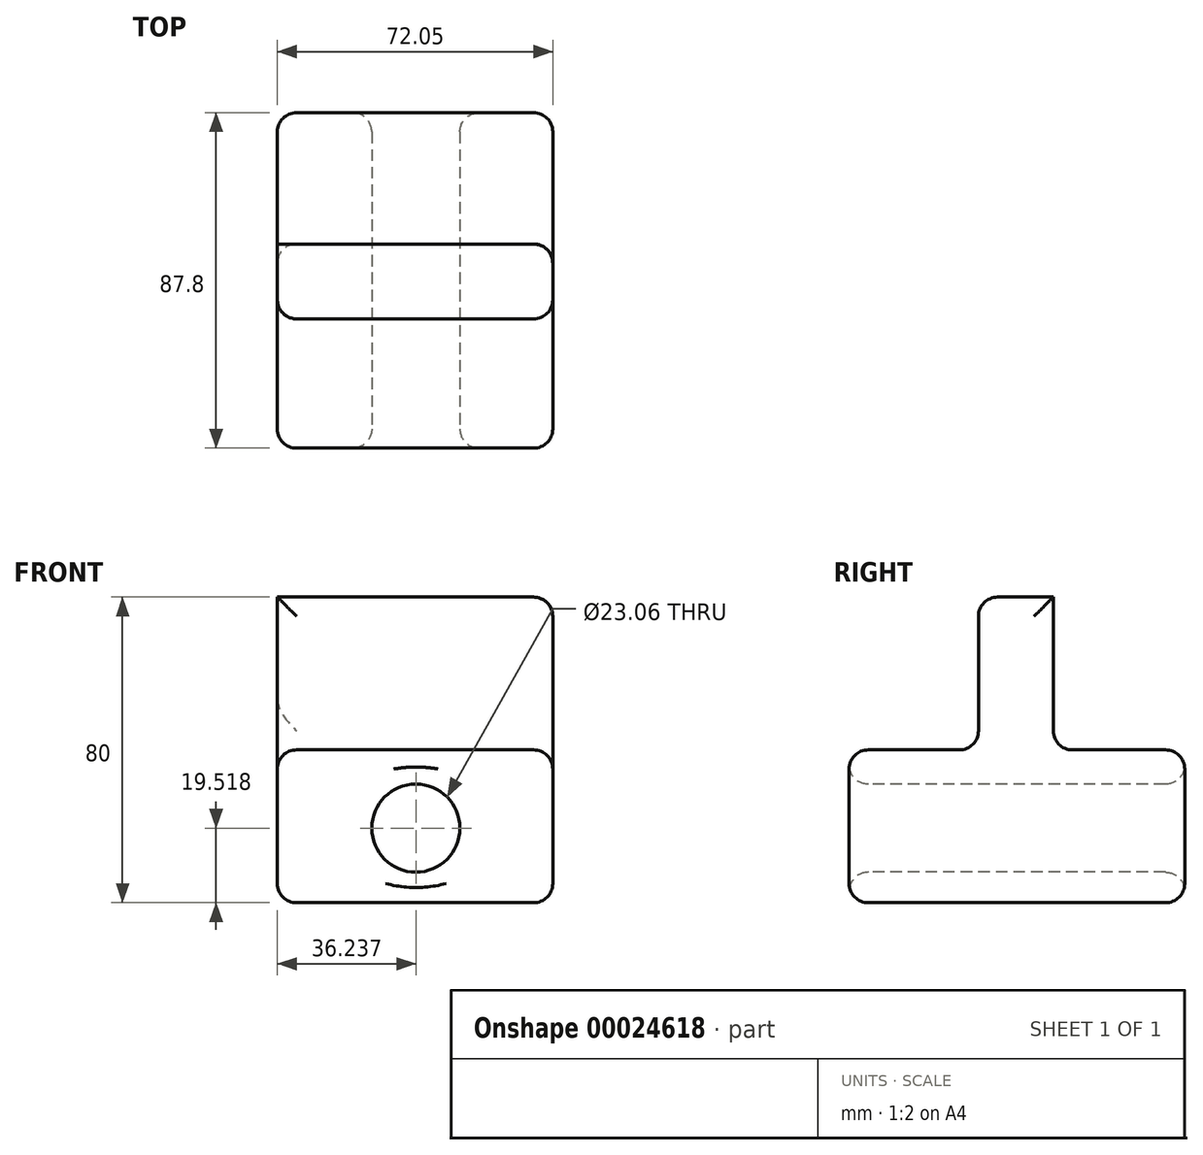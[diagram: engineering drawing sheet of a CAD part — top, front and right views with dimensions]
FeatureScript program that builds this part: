
annotation { "Feature Type Name" : "Feature", "Feature Type Description" : "" }
export const myFeature = defineFeature(function(context is Context, id is Id, definition is map)
    precondition{}
    {
        {
            var Q0;
            Q0=qCreatedBy(makeId("Top.planeOp"),FACE);
            var sketch = newSketch(context, id + "F0", { "sketchPlane" : qUnion([Q0])});
            skLineSegment(sketch, "E0.bottom", {"start": v(-59.89, -44.54) * mm, "end": v(12.16, -44.54) * mm});
            skLineSegment(sketch, "E0.top", {"start": v(-59.89, 43.26) * mm, "end": v(12.16, 43.26) * mm});
            skLineSegment(sketch, "E0.left", {"start": v(-59.89, -44.54) * mm, "end": v(-59.89, 43.26) * mm});
            skLineSegment(sketch, "E0.right", {"start": v(12.16, -44.54) * mm, "end": v(12.16, 43.26) * mm});
            skSolve(sketch);
        }
        {
            var Q0;
            Q0=makeQuery(id+"F0.imprint","IMPRINT",FACE,{"disambiguationData":[TD([[makeQuery(id+"F0.imprint","IMPRINT",EDGE,{"derivedFrom":sQuery(id+"F0.wireOp",EDGE,"E0.bottom")}),1.0]])]});
            extrude(context, id + "F1", {"entities" : qUnion([Q0]), "depth" : 40 * mm});
        }
        {
            var Q0;
            Q0=makeQuery(id+"F1.opExtrude","SWEPT_FACE",FACE,{"disambiguationData":[OSD([sQuery(id+"F0.wireOp",EDGE,"E0.bottom")])]});
            var sketch = newSketch(context, id + "F2", { "sketchPlane" : qUnion([Q0])});
            skCircle(sketch, "E1", {"center": v(-23.65, 19.52) * mm, "radius": 11.53 * mm});
            skSolve(sketch);
        }
        {
            var Q0;
            Q0=makeQuery(id+"F2.imprint","IMPRINT",FACE,{"disambiguationData":[TD([[makeQuery(id+"F2.imprint","IMPRINT",EDGE,{"derivedFrom":sQuery(id+"F2.wireOp",EDGE,"E1")}),1.0]])]});
            extrude(context, id + "F3", {"entities" : qUnion([Q0]), "operationType" : NewBodyOperationType.REMOVE, "endBound" : BoundingType.THROUGH_ALL, "oppositeDirection" : true, "depth" : 25 * mm});
        }
        {
            var Q0;
            Q0=makeQuery(id+"F1.opExtrude","CAP_FACE",FACE,{"disambiguationData":[OSD([sQuery(id+"F0.wireOp",EDGE,"E0.bottom"),sQuery(id+"F0.wireOp",EDGE,"E0.top"),sQuery(id+"F0.wireOp",EDGE,"E0.left"),sQuery(id+"F0.wireOp",EDGE,"E0.right")])],"isStart":false});
            var sketch = newSketch(context, id + "F4", { "sketchPlane" : qUnion([Q0])});
            skLineSegment(sketch, "E2.bottom", {"start": v(-59.89, -10.7) * mm, "end": v(12.16, -10.7) * mm});
            skLineSegment(sketch, "E2.top", {"start": v(-59.89, 8.88) * mm, "end": v(12.16, 8.88) * mm});
            skLineSegment(sketch, "E2.left", {"start": v(-59.89, -10.7) * mm, "end": v(-59.89, 8.88) * mm});
            skLineSegment(sketch, "E2.right", {"start": v(12.16, -10.7) * mm, "end": v(12.16, 8.88) * mm});
            skSolve(sketch);
        }
        {
            var Q0;
            Q0=makeQuery(id+"F4.imprint","IMPRINT",FACE,{"disambiguationData":[TD([[makeQuery(id+"F4.imprint","IMPRINT",EDGE,{"derivedFrom":sQuery(id+"F4.wireOp",EDGE,"E2.bottom")}),1.0]])]});
            extrude(context, id + "F5", {"entities" : qUnion([Q0]), "operationType" : NewBodyOperationType.ADD, "depth" : 40 * mm});
        }
        {
            var Q0;
            Q0=makeQuery(id+"F5.opExtrude","SWEPT_FACE",FACE,{"disambiguationData":[OSD([sQuery(id+"F4.wireOp",EDGE,"E2.bottom")])]});
            var Q1;
            {var subQ0=sQuery(id+"F0.wireOp",EDGE,"E0.bottom");var subQ1=sQuery(id+"F0.wireOp",EDGE,"E0.left");var subQ2=sQuery(id+"F0.wireOp",EDGE,"E0.right");Q1=makeQuery(id+"F5.boolean.opBoolean","SPLIT",FACE,{"disambiguationData":[TD([makeQuery(id+"F1.opExtrude","SWEPT_FACE",FACE,{"disambiguationData":[OSD([subQ0])]})])],"derivedFrom":makeQuery(id+"F1.opExtrude","CAP_FACE",FACE,{"disambiguationData":[OSD([subQ0,sQuery(id+"F0.wireOp",EDGE,"E0.top"),subQ1,subQ2])],"isStart":false})});}
            var Q2;
            Q2=makeQuery(id+"F1.opExtrude","SWEPT_FACE",FACE,{"disambiguationData":[OSD([sQuery(id+"F0.wireOp",EDGE,"E0.bottom")])]});
            var Q3;
            Q3=makeQuery(id+"F3.boolean.opBoolean","COPY",FACE,{"derivedFrom":makeQuery(id+"F3.opExtrude","SWEPT_FACE",FACE,{"disambiguationData":[OSD([sQuery(id+"F2.wireOp",EDGE,"E1")])]})});
            var Q4;
            Q4=makeQuery(id+"F5.boolean.opBoolean","MERGE",FACE,{"derivedFrom":[makeQuery(id+"F1.opExtrude","SWEPT_FACE",FACE,{"disambiguationData":[OSD([sQuery(id+"F0.wireOp",EDGE,"E0.right")])]}),makeQuery(id+"F5.opExtrude","SWEPT_FACE",FACE,{"disambiguationData":[OSD([sQuery(id+"F4.wireOp",EDGE,"E2.right")])]})]});
            var Q5;
            {var subQ0=sQuery(id+"F0.wireOp",EDGE,"E0.top");var subQ1=sQuery(id+"F0.wireOp",EDGE,"E0.left");var subQ2=sQuery(id+"F0.wireOp",EDGE,"E0.right");Q5=makeQuery(id+"F5.boolean.opBoolean","SPLIT",FACE,{"disambiguationData":[TD([makeQuery(id+"F1.opExtrude","SWEPT_FACE",FACE,{"disambiguationData":[OSD([subQ0])]})])],"derivedFrom":makeQuery(id+"F1.opExtrude","CAP_FACE",FACE,{"disambiguationData":[OSD([sQuery(id+"F0.wireOp",EDGE,"E0.bottom"),subQ0,subQ1,subQ2])],"isStart":false})});}
            var Q6;
            Q6=makeQuery(id+"F1.opExtrude","CAP_FACE",FACE,{"disambiguationData":[OSD([sQuery(id+"F0.wireOp",EDGE,"E0.bottom"),sQuery(id+"F0.wireOp",EDGE,"E0.top"),sQuery(id+"F0.wireOp",EDGE,"E0.left"),sQuery(id+"F0.wireOp",EDGE,"E0.right")])],"isStart":true});
            var Q7;
            Q7=makeQuery(id+"F1.opExtrude","SWEPT_FACE",FACE,{"disambiguationData":[OSD([sQuery(id+"F0.wireOp",EDGE,"E0.top")])]});
            fillet(context, id + "F6", {"entities" : qUnion([Q0, Q1, Q2, Q3, Q4, Q5, Q6, Q7]), "radius" : 5 * mm, "tangentPropagation" : true, "allowEdgeOverflow" : false});
        }
    });
